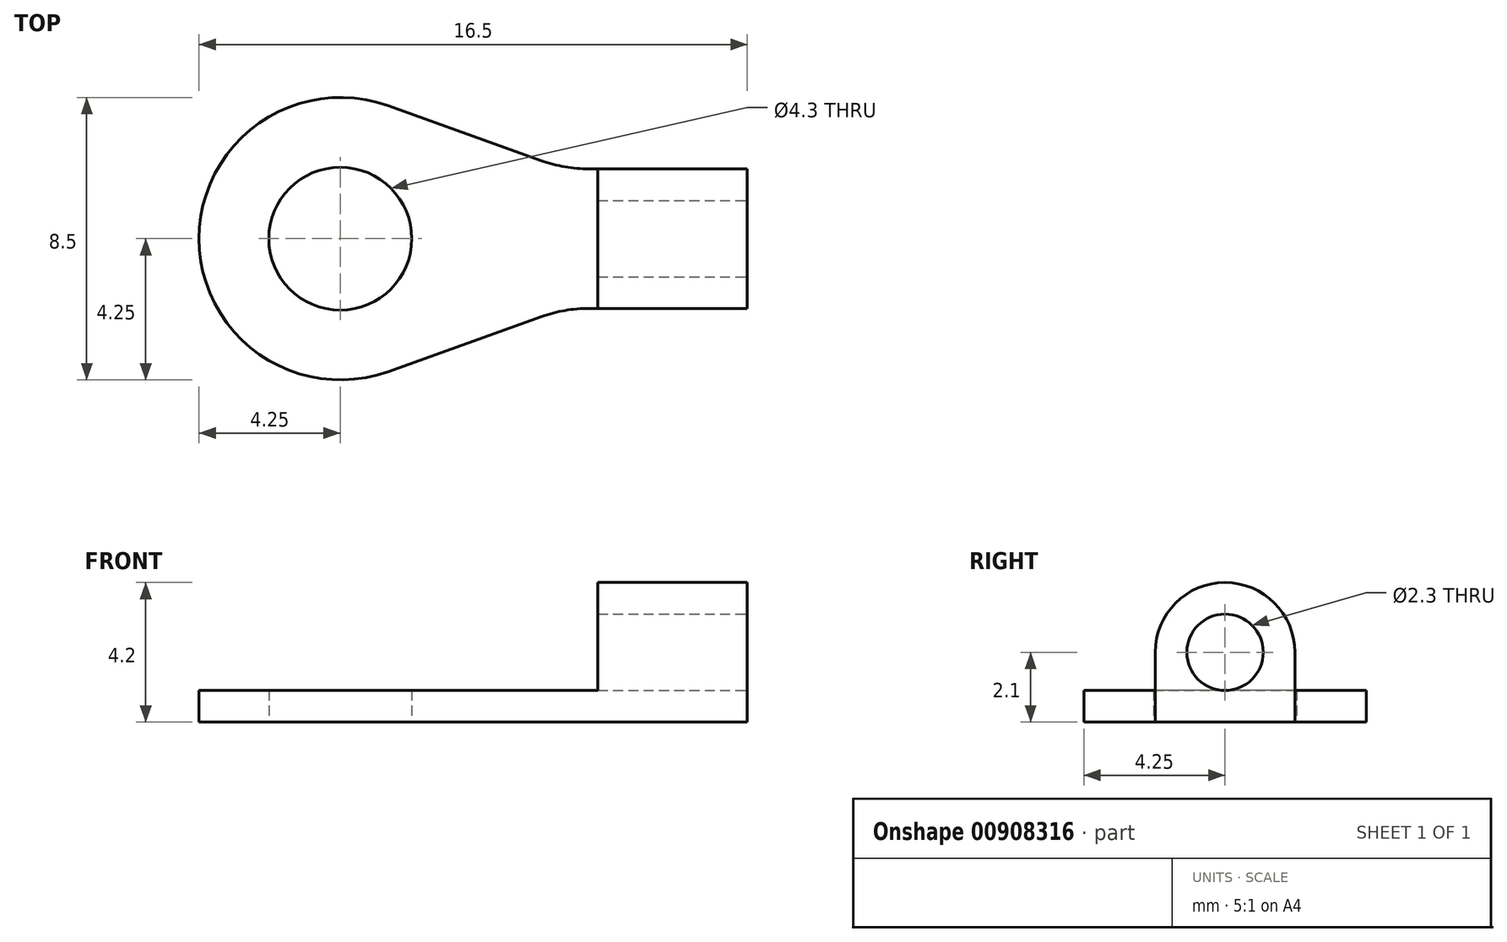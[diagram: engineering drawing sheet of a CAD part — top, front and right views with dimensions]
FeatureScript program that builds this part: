
annotation { "Feature Type Name" : "Feature", "Feature Type Description" : "" }
export const myFeature = defineFeature(function(context is Context, id is Id, definition is map)
    precondition{}
    {
        {
            var Q0;
            Q0=qCreatedBy(makeId("Top.planeOp"),FACE);
            var sketch = newSketch(context, id + "F0", { "sketchPlane" : qUnion([Q0])});
            skLineSegment(sketch, "E0.left", {"start": v(0, 4.25) * mm, "end": v(0, 4.25) * mm});
            skLineSegment(sketch, "E0.right", {"start": v(16.5, 2.15) * mm, "end": v(16.5, 6.35) * mm});
            skPoint(sketch, "E1.visualSharp", {"position": v(0, 8.5) * mm});
            skArc(sketch, "E1.filletArc", {"start": v(4.25, 8.5) * mm, "mid": v(1.24, 7.26) * mm, "end": v(0, 4.25) * mm});
            skPoint(sketch, "E2.visualSharp", {"position": v(0, 0) * mm});
            skArc(sketch, "E2.filletArc", {"start": v(0, 4.25) * mm, "mid": v(1.24, 1.24) * mm, "end": v(4.25, 0) * mm});
            skLineSegment(sketch, "E3.bottom", {"start": v(16.5, 2.15) * mm, "end": v(11.74, 2.15) * mm});
            skLineSegment(sketch, "E3.top", {"start": v(16.5, 6.35) * mm, "end": v(11.74, 6.35) * mm});
            skPoint(sketch, "E3.middle", {"position": v(16.5, 4.25) * mm});
            skArc(sketch, "E4", {"start": v(5.68, 8.25) * mm, "mid": v(0, 4.25) * mm, "end": v(5.68, 0.25) * mm});
            skCircle(sketch, "E5", {"center": v(4.25, 4.25) * mm, "radius": 2.15 * mm});
            skLineSegment(sketch, "E6", {"start": v(10.3, 6.6) * mm, "end": v(5.68, 8.25) * mm});
            skLineSegment(sketch, "E7", {"start": v(10.3, 1.9) * mm, "end": v(5.68, 0.25) * mm});
            skPoint(sketch, "E8.visualSharp", {"position": v(11, 6.35) * mm});
            skArc(sketch, "E8.filletArc", {"start": v(10.3, 6.6) * mm, "mid": v(11.01, 6.41) * mm, "end": v(11.74, 6.35) * mm});
            skPoint(sketch, "E9.visualSharp", {"position": v(11, 2.15) * mm});
            skArc(sketch, "E9.filletArc", {"start": v(11.74, 2.15) * mm, "mid": v(11.01, 2.09) * mm, "end": v(10.3, 1.9) * mm});
            skPoint(sketch, "E3.left.end.orphan", {"position": v(21, 6.35) * mm});
            skPoint(sketch, "E10.orphan", {"position": v(21, 2.15) * mm});
            skPoint(sketch, "E0.bottom.end.orphan", {"position": v(16.5, 0) * mm});
            skPoint(sketch, "E0.top.end.orphan", {"position": v(16.5, 8.5) * mm});
            skPoint(sketch, "E3.right.end.orphan", {"position": v(12, 6.35) * mm});
            skPoint(sketch, "E3.right.start.orphan", {"position": v(12, 2.15) * mm});
            skSolve(sketch);
        }
        {
            var Q0;
            Q0=makeQuery(id+"F0.imprint","IMPRINT",FACE,{"disambiguationData":[TD([[makeQuery(id+"F0.imprint","IMPRINT",EDGE,{"derivedFrom":sQuery(id+"F0.wireOp",EDGE,"E0.right")}),1.0]])]});
            extrude(context, id + "F1", {"entities" : qUnion([Q0]), "depth" : .95 * mm, "offsetDistance" : 25 * mm});
        }
        {
            var Q0;
            Q0=makeQuery(id+"F1.opExtrude","CAP_FACE",FACE,{"disambiguationData":[OSD([sQuery(id+"F0.wireOp",EDGE,"E0.right"),sQuery(id+"F0.wireOp",EDGE,"E3.bottom"),sQuery(id+"F0.wireOp",EDGE,"E3.top"),sQuery(id+"F0.wireOp",EDGE,"E4"),sQuery(id+"F0.wireOp",EDGE,"E5"),sQuery(id+"F0.wireOp",EDGE,"E6"),sQuery(id+"F0.wireOp",EDGE,"E7"),sQuery(id+"F0.wireOp",EDGE,"E8.filletArc"),sQuery(id+"F0.wireOp",EDGE,"E9.filletArc")])],"isStart":false});
            var sketch = newSketch(context, id + "F2", { "sketchPlane" : qUnion([Q0])});
            skLineSegment(sketch, "E11.bottom", {"start": v(16.5, 6.35) * mm, "end": v(12, 6.35) * mm});
            skLineSegment(sketch, "E11.top", {"start": v(16.5, 2.15) * mm, "end": v(12, 2.15) * mm});
            skLineSegment(sketch, "E11.left", {"start": v(16.5, 6.35) * mm, "end": v(16.5, 2.15) * mm});
            skLineSegment(sketch, "E11.right", {"start": v(12, 6.35) * mm, "end": v(12, 2.15) * mm});
            skSolve(sketch);
        }
        {
            var Q0;
            Q0=makeQuery(id+"F2.imprint","IMPRINT",FACE,{"disambiguationData":[TD([[makeQuery(id+"F2.imprint","IMPRINT",EDGE,{"derivedFrom":sQuery(id+"F2.wireOp",EDGE,"E11.bottom")}),1.0]])]});
            extrude(context, id + "F3", {"entities" : qUnion([Q0]), "operationType" : NewBodyOperationType.ADD, "depth" : 3.25 * mm, "offsetDistance" : 25 * mm});
        }
        {
            var Q0;
            Q0=makeQuery(id+"F3.opExtrude","CAP_EDGE",EDGE,{"disambiguationData":[OSD([sQuery(id+"F2.wireOp",EDGE,"E11.bottom")])],"isStart":false});
            var Q1;
            Q1=makeQuery(id+"F3.opExtrude","CAP_EDGE",EDGE,{"disambiguationData":[OSD([sQuery(id+"F2.wireOp",EDGE,"E11.top")])],"isStart":false});
            fillet(context, id + "F4", {"entities" : qUnion([Q0, Q1]), "radius" : 2.1 * mm, "tangentPropagation" : true, "allowEdgeOverflow" : false});
        }
        {
            var Q0;
            Q0=makeQuery(id+"F3.boolean.opBoolean","MERGE",FACE,{"derivedFrom":[makeQuery(id+"F1.opExtrude","SWEPT_FACE",FACE,{"disambiguationData":[OSD([sQuery(id+"F0.wireOp",EDGE,"E0.right")])]}),makeQuery(id+"F3.opExtrude","SWEPT_FACE",FACE,{"disambiguationData":[OSD([sQuery(id+"F2.wireOp",EDGE,"E11.left")])]})]});
            var sketch = newSketch(context, id + "F5", { "sketchPlane" : qUnion([Q0])});
            skCircle(sketch, "E12", {"center": v(4.25, 2.1) * mm, "radius": 1.15 * mm});
            skSolve(sketch);
        }
        {
            var Q0;
            Q0=makeQuery(id+"F5.imprint","IMPRINT",FACE,{"disambiguationData":[TD([[makeQuery(id+"F5.imprint","IMPRINT",EDGE,{"derivedFrom":sQuery(id+"F5.wireOp",EDGE,"E12")}),1.0]])]});
            extrude(context, id + "F6", {"entities" : qUnion([Q0]), "operationType" : NewBodyOperationType.REMOVE, "oppositeDirection" : true, "depth" : 25 * mm, "offsetDistance" : 25 * mm});
        }
    });
